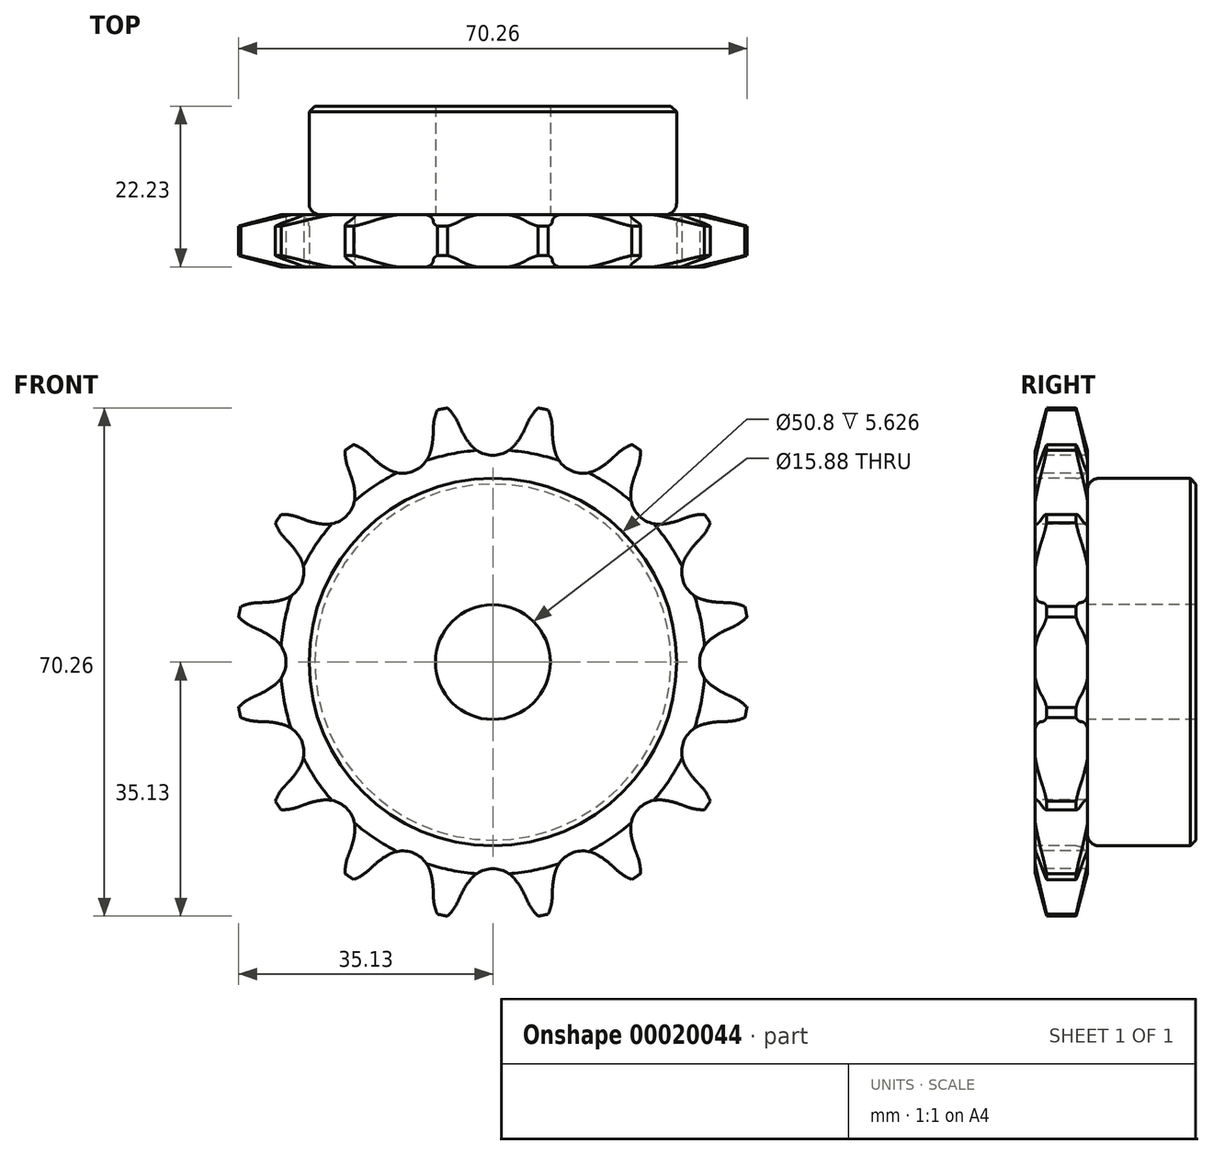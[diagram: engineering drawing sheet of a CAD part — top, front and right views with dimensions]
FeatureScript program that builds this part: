
annotation { "Feature Type Name" : "Feature", "Feature Type Description" : "" }
export const myFeature = defineFeature(function(context is Context, id is Id, definition is map)
    precondition{}
    {
        {
            var Q0;
            Q0=qCreatedBy(makeId("Right.planeOp"),FACE);
            var sketch = newSketch(context, id + "F0", { "sketchPlane" : qUnion([Q0])});
            skLineSegment(sketch, "E0", {"start": v(0, 0) * mm, "end": v(32.17, 0) * mm, "construction": true});
            skLineSegment(sketch, "E1.bottom", {"start": v(0, 7.94) * mm, "end": v(7.21, 7.94) * mm});
            skLineSegment(sketch, "E1.top", {"start": v(0, 35.69) * mm, "end": v(7.21, 35.69) * mm});
            skLineSegment(sketch, "E1.left", {"start": v(0, 7.94) * mm, "end": v(0, 35.69) * mm});
            skLineSegment(sketch, "E1.right", {"start": v(7.21, 7.94) * mm, "end": v(7.21, 35.69) * mm});
            skLineSegment(sketch, "E2.bottom", {"start": v(0, 7.94) * mm, "end": v(22.23, 7.94) * mm});
            skLineSegment(sketch, "E2.top", {"start": v(0, 25.4) * mm, "end": v(22.23, 25.4) * mm});
            skLineSegment(sketch, "E2.left", {"start": v(0, 7.94) * mm, "end": v(0, 25.4) * mm});
            skLineSegment(sketch, "E2.right", {"start": v(22.23, 7.94) * mm, "end": v(22.23, 25.4) * mm});
            skLineSegment(sketch, "E3.MirrorCS", {"start": v(0, -7.94) * mm, "end": v(0, -25.4) * mm});
            skLineSegment(sketch, "E4.MirrorCS", {"start": v(0, -7.94) * mm, "end": v(7.21, -7.94) * mm});
            skLineSegment(sketch, "E5.MirrorCS", {"start": v(0, -35.69) * mm, "end": v(7.21, -35.69) * mm});
            skLineSegment(sketch, "E6.MirrorCS", {"start": v(0, -7.94) * mm, "end": v(0, -35.69) * mm});
            skLineSegment(sketch, "E7.MirrorCS", {"start": v(7.21, -7.94) * mm, "end": v(7.21, -35.69) * mm});
            skLineSegment(sketch, "E8.MirrorCS", {"start": v(0, -7.94) * mm, "end": v(22.23, -7.94) * mm});
            skLineSegment(sketch, "E9.MirrorCS", {"start": v(0, -25.4) * mm, "end": v(22.23, -25.4) * mm});
            skLineSegment(sketch, "E10.MirrorCS", {"start": v(22.23, -7.94) * mm, "end": v(22.23, -25.4) * mm});
            skSolve(sketch);
        }
        {
            var Q0;
            {var subQ0=sQuery(id+"F0.wireOp",EDGE,"E2.left");Q0=makeQuery(id+"F0.imprint","IMPRINT",FACE,{"disambiguationData":[TD([[makeQuery(id+"F0.imprint","IMPRINT",EDGE,{"derivedFrom":subQ0}),-1.0]])]});}
            var Q1;
            {var subQ4=sQuery(id+"F0.wireOp",EDGE,"E1.top");Q1=makeQuery(id+"F0.imprint","IMPRINT",FACE,{"disambiguationData":[TD([[makeQuery(id+"F0.imprint","IMPRINT",EDGE,{"derivedFrom":subQ4}),-1.0]])]});}
            var Q2;
            {var subQ0=sQuery(id+"F0.wireOp",EDGE,"E2.right");Q2=makeQuery(id+"F0.imprint","IMPRINT",FACE,{"disambiguationData":[TD([[makeQuery(id+"F0.imprint","IMPRINT",EDGE,{"derivedFrom":subQ0}),1.0]])]});}
            var Q3;
            Q3=sQuery(id+"F0.wireOp",EDGE,"E0");
            revolve(context, id + "F1", {"entities" : qUnion([Q0, Q1, Q2]), "axis" : qUnion([Q3]), "revolveType" : RevolveType.FULL});
        }
        {
            var Q0;
            Q0=makeQuery(id+"F1.opRevolve","SWEPT_EDGE",EDGE,{"disambiguationData":[OSD([sQuery(id+"F0.wireOp",EDGE,"E1.right"),sQuery(id+"F0.wireOp",EDGE,"E2.top")])]});
            fillet(context, id + "F2", {"entities" : qUnion([Q0]), "radius" : 1.59 * mm, "tangentPropagation" : true, "allowEdgeOverflow" : false});
        }
        {
            var Q0;
            Q0=makeQuery(id+"F1.opRevolve","SWEPT_EDGE",EDGE,{"disambiguationData":[OSD([sQuery(id+"F0.wireOp",EDGE,"E2.top"),sQuery(id+"F0.wireOp",EDGE,"E2.right")])]});
            chamfer(context, id + "F3", {"entities" : qUnion([Q0]), "width" : 0.8 * mm, "tangentPropagation" : true});
        }
        {
            var Q0;
            Q0=makeQuery(id+"F1.opRevolve","SWEPT_EDGE",EDGE,{"disambiguationData":[OSD([sQuery(id+"F0.wireOp",EDGE,"E1.top"),sQuery(id+"F0.wireOp",EDGE,"E1.left")])]});
            var Q1;
            Q1=makeQuery(id+"F1.opRevolve","SWEPT_EDGE",EDGE,{"disambiguationData":[OSD([sQuery(id+"F0.wireOp",EDGE,"E1.top"),sQuery(id+"F0.wireOp",EDGE,"E1.right")])]});
            chamfer(context, id + "F4", {"entities" : qUnion([Q0, Q1]), "chamferType" : ChamferType.TWO_OFFSETS, "width1" : 6.35 * mm, "oppositeDirection" : false, "width2" : 1.57 * mm, "tangentPropagation" : true});
        }
        {
            var Q0;
            Q0=makeQuery(id+"F1.opRevolve","SWEPT_FACE",FACE,{"disambiguationData":[OSD([sQuery(id+"F0.wireOp",EDGE,"E1.left"),sQuery(id+"F0.wireOp",EDGE,"E2.left")])]});
            var sketch = newSketch(context, id + "F5", { "sketchPlane" : qUnion([Q0])});
            skCircle(sketch, "E11", {"center": v(0, 0) * mm, "radius": 32.55 * mm, "construction": true});
            skLineSegment(sketch, "E12", {"start": v(0, 0) * mm, "end": v(0, 32.55) * mm, "construction": true});
            skLineSegment(sketch, "E13", {"start": v(0, 32.55) * mm, "end": v(21.93, 32.55) * mm, "construction": true});
            skLineSegment(sketch, "E14", {"start": v(0, 32.55) * mm, "end": v(4.99, 36.55) * mm, "construction": true});
            skLineSegment(sketch, "E15", {"start": v(4.99, 36.55) * mm, "end": v(-4.46, 32.3) * mm, "construction": true});
            skLineSegment(sketch, "E16", {"start": v(-4.46, 32.3) * mm, "end": v(-4.81, 33.1) * mm});
            skLineSegment(sketch, "E17", {"start": v(0, 0) * mm, "end": v(-7.13, 35.84) * mm, "construction": true});
            skArc(sketch, "E18", {"start": v(-7.13, 35.84) * mm, "mid": v(-15.86, 26.14) * mm, "end": v(-4.81, 33.1) * mm, "construction": true});
            skArc(sketch, "E19", {"start": v(-4.81, 33.1) * mm, "mid": v(-5.78, 34.63) * mm, "end": v(-7.13, 35.84) * mm});
            skLineSegment(sketch, "E20", {"start": v(-4.81, 33.1) * mm, "end": v(-4.81, 33.1) * mm});
            skLineSegment(sketch, "E21", {"start": v(-4.81, 33.1) * mm, "end": v(-5.93, 35.58) * mm, "construction": true});
            skArc(sketch, "E22", {"start": v(-4.46, 32.3) * mm, "mid": v(-3.84, 31.14) * mm, "end": v(-3.1, 30.07) * mm});
            skArc(sketch, "E23", {"start": v(-3.1, 30.07) * mm, "mid": v(13.82, 41.97) * mm, "end": v(-4.46, 32.3) * mm, "construction": true});
            skArc(sketch, "E24.MirrorCS", {"start": v(4.81, 33.1) * mm, "mid": v(5.78, 34.63) * mm, "end": v(7.13, 35.84) * mm});
            skLineSegment(sketch, "E25.MirrorCS", {"start": v(4.46, 32.3) * mm, "end": v(4.81, 33.1) * mm});
            skArc(sketch, "E26.MirrorCS", {"start": v(4.46, 32.3) * mm, "mid": v(3.84, 31.14) * mm, "end": v(3.1, 30.07) * mm});
            skArc(sketch, "E27", {"start": v(-3.1, 30.07) * mm, "mid": v(0, 28.59) * mm, "end": v(3.1, 30.07) * mm});
            skArc(sketch, "E28", {"start": v(3.1, 30.07) * mm, "mid": v(0, 36.51) * mm, "end": v(-3.1, 30.07) * mm, "construction": true});
            skLineSegment(sketch, "E29.1.0", {"start": v(-16.48, 28.13) * mm, "end": v(-17.11, 28.73) * mm});
            skArc(sketch, "E29.1.1", {"start": v(-17.11, 28.73) * mm, "mid": v(-18.6, 29.78) * mm, "end": v(-20.3, 30.39) * mm});
            skArc(sketch, "E29.1.2", {"start": v(-16.48, 28.13) * mm, "mid": v(-15.47, 27.3) * mm, "end": v(-14.36, 26.6) * mm});
            skArc(sketch, "E29.1.3", {"start": v(-14.36, 26.6) * mm, "mid": v(-10.94, 26.41) * mm, "end": v(-8.65, 28.96) * mm});
            skArc(sketch, "E29.1.4", {"start": v(-8.24, 31.55) * mm, "mid": v(-8.37, 30.24) * mm, "end": v(-8.65, 28.96) * mm});
            skLineSegment(sketch, "E29.1.5", {"start": v(-8.24, 31.55) * mm, "end": v(-8.22, 32.41) * mm});
            skArc(sketch, "E29.1.6", {"start": v(-8.22, 32.41) * mm, "mid": v(-7.91, 34.2) * mm, "end": v(-7.13, 35.84) * mm});
            skLineSegment(sketch, "E29.2.0", {"start": v(-25.99, 19.69) * mm, "end": v(-26.8, 20) * mm});
            skArc(sketch, "E29.2.1", {"start": v(-26.8, 20) * mm, "mid": v(-28.57, 20.4) * mm, "end": v(-30.39, 20.3) * mm});
            skArc(sketch, "E29.2.2", {"start": v(-25.99, 19.69) * mm, "mid": v(-24.74, 19.3) * mm, "end": v(-23.45, 19.08) * mm});
            skArc(sketch, "E29.2.3", {"start": v(-23.45, 19.08) * mm, "mid": v(-20.21, 20.21) * mm, "end": v(-19.08, 23.45) * mm});
            skArc(sketch, "E29.2.4", {"start": v(-19.69, 25.99) * mm, "mid": v(-19.3, 24.74) * mm, "end": v(-19.08, 23.45) * mm});
            skLineSegment(sketch, "E29.2.5", {"start": v(-19.69, 25.99) * mm, "end": v(-20, 26.8) * mm});
            skArc(sketch, "E29.2.6", {"start": v(-20, 26.8) * mm, "mid": v(-20.4, 28.57) * mm, "end": v(-20.3, 30.39) * mm});
            skLineSegment(sketch, "E30.1.3.0", {"start": v(-31.55, 8.24) * mm, "end": v(-32.41, 8.22) * mm});
            skArc(sketch, "E30.3.3.0", {"start": v(-32.41, 8.22) * mm, "mid": v(-34.2, 7.91) * mm, "end": v(-35.84, 7.13) * mm});
            skArc(sketch, "E30.7.3.0", {"start": v(-31.55, 8.24) * mm, "mid": v(-30.24, 8.37) * mm, "end": v(-28.96, 8.65) * mm});
            skArc(sketch, "E30.11.3.0", {"start": v(-28.96, 8.65) * mm, "mid": v(-26.41, 10.94) * mm, "end": v(-26.6, 14.36) * mm});
            skArc(sketch, "E30.15.3.0", {"start": v(-28.13, 16.48) * mm, "mid": v(-27.3, 15.47) * mm, "end": v(-26.6, 14.36) * mm});
            skLineSegment(sketch, "E30.19.3.0", {"start": v(-28.13, 16.48) * mm, "end": v(-28.73, 17.11) * mm});
            skArc(sketch, "E30.22.3.0", {"start": v(-28.73, 17.11) * mm, "mid": v(-29.78, 18.6) * mm, "end": v(-30.39, 20.3) * mm});
            skLineSegment(sketch, "E30.1.4.0", {"start": v(-32.3, -4.46) * mm, "end": v(-33.1, -4.81) * mm});
            skArc(sketch, "E30.3.4.0", {"start": v(-33.1, -4.81) * mm, "mid": v(-34.63, -5.78) * mm, "end": v(-35.84, -7.13) * mm});
            skArc(sketch, "E30.7.4.0", {"start": v(-32.3, -4.46) * mm, "mid": v(-31.14, -3.84) * mm, "end": v(-30.07, -3.1) * mm});
            skArc(sketch, "E30.11.4.0", {"start": v(-30.07, -3.1) * mm, "mid": v(-28.59, 0) * mm, "end": v(-30.07, 3.1) * mm});
            skArc(sketch, "E30.15.4.0", {"start": v(-32.3, 4.46) * mm, "mid": v(-31.14, 3.84) * mm, "end": v(-30.07, 3.1) * mm});
            skLineSegment(sketch, "E30.19.4.0", {"start": v(-32.3, 4.46) * mm, "end": v(-33.1, 4.81) * mm});
            skArc(sketch, "E30.22.4.0", {"start": v(-33.1, 4.81) * mm, "mid": v(-34.63, 5.78) * mm, "end": v(-35.84, 7.13) * mm});
            skLineSegment(sketch, "E30.1.5.0", {"start": v(-28.13, -16.48) * mm, "end": v(-28.73, -17.11) * mm});
            skArc(sketch, "E30.3.5.0", {"start": v(-28.73, -17.11) * mm, "mid": v(-29.78, -18.6) * mm, "end": v(-30.39, -20.3) * mm});
            skArc(sketch, "E30.7.5.0", {"start": v(-28.13, -16.48) * mm, "mid": v(-27.3, -15.47) * mm, "end": v(-26.6, -14.36) * mm});
            skArc(sketch, "E30.11.5.0", {"start": v(-26.6, -14.36) * mm, "mid": v(-26.41, -10.94) * mm, "end": v(-28.96, -8.65) * mm});
            skArc(sketch, "E30.15.5.0", {"start": v(-31.55, -8.24) * mm, "mid": v(-30.24, -8.37) * mm, "end": v(-28.96, -8.65) * mm});
            skLineSegment(sketch, "E30.19.5.0", {"start": v(-31.55, -8.24) * mm, "end": v(-32.41, -8.22) * mm});
            skArc(sketch, "E30.22.5.0", {"start": v(-32.41, -8.22) * mm, "mid": v(-34.2, -7.91) * mm, "end": v(-35.84, -7.13) * mm});
            skLineSegment(sketch, "E30.1.6.0", {"start": v(-19.69, -25.99) * mm, "end": v(-20, -26.8) * mm});
            skArc(sketch, "E30.3.6.0", {"start": v(-20, -26.8) * mm, "mid": v(-20.4, -28.57) * mm, "end": v(-20.3, -30.39) * mm});
            skArc(sketch, "E30.7.6.0", {"start": v(-19.69, -25.99) * mm, "mid": v(-19.3, -24.74) * mm, "end": v(-19.08, -23.45) * mm});
            skArc(sketch, "E30.11.6.0", {"start": v(-19.08, -23.45) * mm, "mid": v(-20.21, -20.21) * mm, "end": v(-23.45, -19.08) * mm});
            skArc(sketch, "E30.15.6.0", {"start": v(-25.99, -19.69) * mm, "mid": v(-24.74, -19.3) * mm, "end": v(-23.45, -19.08) * mm});
            skLineSegment(sketch, "E30.19.6.0", {"start": v(-25.99, -19.69) * mm, "end": v(-26.8, -20) * mm});
            skArc(sketch, "E30.22.6.0", {"start": v(-26.8, -20) * mm, "mid": v(-28.57, -20.4) * mm, "end": v(-30.39, -20.3) * mm});
            skLineSegment(sketch, "E30.1.7.0", {"start": v(-8.24, -31.55) * mm, "end": v(-8.22, -32.41) * mm});
            skArc(sketch, "E30.3.7.0", {"start": v(-8.22, -32.41) * mm, "mid": v(-7.91, -34.2) * mm, "end": v(-7.13, -35.84) * mm});
            skArc(sketch, "E30.7.7.0", {"start": v(-8.24, -31.55) * mm, "mid": v(-8.37, -30.24) * mm, "end": v(-8.65, -28.96) * mm});
            skArc(sketch, "E30.11.7.0", {"start": v(-8.65, -28.96) * mm, "mid": v(-10.94, -26.41) * mm, "end": v(-14.36, -26.6) * mm});
            skArc(sketch, "E30.15.7.0", {"start": v(-16.48, -28.13) * mm, "mid": v(-15.47, -27.3) * mm, "end": v(-14.36, -26.6) * mm});
            skLineSegment(sketch, "E30.19.7.0", {"start": v(-16.48, -28.13) * mm, "end": v(-17.11, -28.73) * mm});
            skArc(sketch, "E30.22.7.0", {"start": v(-17.11, -28.73) * mm, "mid": v(-18.6, -29.78) * mm, "end": v(-20.3, -30.39) * mm});
            skLineSegment(sketch, "E30.1.8.0", {"start": v(4.46, -32.3) * mm, "end": v(4.81, -33.1) * mm});
            skArc(sketch, "E30.3.8.0", {"start": v(4.81, -33.1) * mm, "mid": v(5.78, -34.63) * mm, "end": v(7.13, -35.84) * mm});
            skArc(sketch, "E30.7.8.0", {"start": v(4.46, -32.3) * mm, "mid": v(3.84, -31.14) * mm, "end": v(3.1, -30.07) * mm});
            skArc(sketch, "E30.11.8.0", {"start": v(3.1, -30.07) * mm, "mid": v(0, -28.59) * mm, "end": v(-3.1, -30.07) * mm});
            skArc(sketch, "E30.15.8.0", {"start": v(-4.46, -32.3) * mm, "mid": v(-3.84, -31.14) * mm, "end": v(-3.1, -30.07) * mm});
            skLineSegment(sketch, "E30.19.8.0", {"start": v(-4.46, -32.3) * mm, "end": v(-4.81, -33.1) * mm});
            skArc(sketch, "E30.22.8.0", {"start": v(-4.81, -33.1) * mm, "mid": v(-5.78, -34.63) * mm, "end": v(-7.13, -35.84) * mm});
            skLineSegment(sketch, "E30.1.9.0", {"start": v(16.48, -28.13) * mm, "end": v(17.11, -28.73) * mm});
            skArc(sketch, "E30.3.9.0", {"start": v(17.11, -28.73) * mm, "mid": v(18.6, -29.78) * mm, "end": v(20.3, -30.39) * mm});
            skArc(sketch, "E30.7.9.0", {"start": v(16.48, -28.13) * mm, "mid": v(15.47, -27.3) * mm, "end": v(14.36, -26.6) * mm});
            skArc(sketch, "E30.11.9.0", {"start": v(14.36, -26.6) * mm, "mid": v(10.94, -26.41) * mm, "end": v(8.65, -28.96) * mm});
            skArc(sketch, "E30.15.9.0", {"start": v(8.24, -31.55) * mm, "mid": v(8.37, -30.24) * mm, "end": v(8.65, -28.96) * mm});
            skLineSegment(sketch, "E30.19.9.0", {"start": v(8.24, -31.55) * mm, "end": v(8.22, -32.41) * mm});
            skArc(sketch, "E30.22.9.0", {"start": v(8.22, -32.41) * mm, "mid": v(7.91, -34.2) * mm, "end": v(7.13, -35.84) * mm});
            skLineSegment(sketch, "E30.1.10.0", {"start": v(25.99, -19.69) * mm, "end": v(26.8, -20) * mm});
            skArc(sketch, "E30.3.10.0", {"start": v(26.8, -20) * mm, "mid": v(28.57, -20.4) * mm, "end": v(30.39, -20.3) * mm});
            skArc(sketch, "E30.7.10.0", {"start": v(25.99, -19.69) * mm, "mid": v(24.74, -19.3) * mm, "end": v(23.45, -19.08) * mm});
            skArc(sketch, "E30.11.10.0", {"start": v(23.45, -19.08) * mm, "mid": v(20.21, -20.21) * mm, "end": v(19.08, -23.45) * mm});
            skArc(sketch, "E30.15.10.0", {"start": v(19.69, -25.99) * mm, "mid": v(19.3, -24.74) * mm, "end": v(19.08, -23.45) * mm});
            skLineSegment(sketch, "E30.19.10.0", {"start": v(19.69, -25.99) * mm, "end": v(20, -26.8) * mm});
            skArc(sketch, "E30.22.10.0", {"start": v(20, -26.8) * mm, "mid": v(20.4, -28.57) * mm, "end": v(20.3, -30.39) * mm});
            skLineSegment(sketch, "E30.1.11.0", {"start": v(31.55, -8.24) * mm, "end": v(32.41, -8.22) * mm});
            skArc(sketch, "E30.3.11.0", {"start": v(32.41, -8.22) * mm, "mid": v(34.2, -7.91) * mm, "end": v(35.84, -7.13) * mm});
            skArc(sketch, "E30.7.11.0", {"start": v(31.55, -8.24) * mm, "mid": v(30.24, -8.37) * mm, "end": v(28.96, -8.65) * mm});
            skArc(sketch, "E30.11.11.0", {"start": v(28.96, -8.65) * mm, "mid": v(26.41, -10.94) * mm, "end": v(26.6, -14.36) * mm});
            skArc(sketch, "E30.15.11.0", {"start": v(28.13, -16.48) * mm, "mid": v(27.3, -15.47) * mm, "end": v(26.6, -14.36) * mm});
            skLineSegment(sketch, "E30.19.11.0", {"start": v(28.13, -16.48) * mm, "end": v(28.73, -17.11) * mm});
            skArc(sketch, "E30.22.11.0", {"start": v(28.73, -17.11) * mm, "mid": v(29.78, -18.6) * mm, "end": v(30.39, -20.3) * mm});
            skLineSegment(sketch, "E30.1.12.0", {"start": v(32.3, 4.46) * mm, "end": v(33.1, 4.81) * mm});
            skArc(sketch, "E30.3.12.0", {"start": v(33.1, 4.81) * mm, "mid": v(34.63, 5.78) * mm, "end": v(35.84, 7.13) * mm});
            skArc(sketch, "E30.7.12.0", {"start": v(32.3, 4.46) * mm, "mid": v(31.14, 3.84) * mm, "end": v(30.07, 3.1) * mm});
            skArc(sketch, "E30.11.12.0", {"start": v(30.07, 3.1) * mm, "mid": v(28.59, 0) * mm, "end": v(30.07, -3.1) * mm});
            skArc(sketch, "E30.15.12.0", {"start": v(32.3, -4.46) * mm, "mid": v(31.14, -3.84) * mm, "end": v(30.07, -3.1) * mm});
            skLineSegment(sketch, "E30.19.12.0", {"start": v(32.3, -4.46) * mm, "end": v(33.1, -4.81) * mm});
            skArc(sketch, "E30.22.12.0", {"start": v(33.1, -4.81) * mm, "mid": v(34.63, -5.78) * mm, "end": v(35.84, -7.13) * mm});
            skLineSegment(sketch, "E30.1.13.0", {"start": v(28.13, 16.48) * mm, "end": v(28.73, 17.11) * mm});
            skArc(sketch, "E30.3.13.0", {"start": v(28.73, 17.11) * mm, "mid": v(29.78, 18.6) * mm, "end": v(30.39, 20.3) * mm});
            skArc(sketch, "E30.7.13.0", {"start": v(28.13, 16.48) * mm, "mid": v(27.3, 15.47) * mm, "end": v(26.6, 14.36) * mm});
            skArc(sketch, "E30.11.13.0", {"start": v(26.6, 14.36) * mm, "mid": v(26.41, 10.94) * mm, "end": v(28.96, 8.65) * mm});
            skArc(sketch, "E30.15.13.0", {"start": v(31.55, 8.24) * mm, "mid": v(30.24, 8.37) * mm, "end": v(28.96, 8.65) * mm});
            skLineSegment(sketch, "E30.19.13.0", {"start": v(31.55, 8.24) * mm, "end": v(32.41, 8.22) * mm});
            skArc(sketch, "E30.22.13.0", {"start": v(32.41, 8.22) * mm, "mid": v(34.2, 7.91) * mm, "end": v(35.84, 7.13) * mm});
            skLineSegment(sketch, "E30.1.14.0", {"start": v(19.69, 25.99) * mm, "end": v(20, 26.8) * mm});
            skArc(sketch, "E30.3.14.0", {"start": v(20, 26.8) * mm, "mid": v(20.4, 28.57) * mm, "end": v(20.3, 30.39) * mm});
            skArc(sketch, "E30.7.14.0", {"start": v(19.69, 25.99) * mm, "mid": v(19.3, 24.74) * mm, "end": v(19.08, 23.45) * mm});
            skArc(sketch, "E30.11.14.0", {"start": v(19.08, 23.45) * mm, "mid": v(20.21, 20.21) * mm, "end": v(23.45, 19.08) * mm});
            skArc(sketch, "E30.15.14.0", {"start": v(25.99, 19.69) * mm, "mid": v(24.74, 19.3) * mm, "end": v(23.45, 19.08) * mm});
            skLineSegment(sketch, "E30.19.14.0", {"start": v(25.99, 19.69) * mm, "end": v(26.8, 20) * mm});
            skArc(sketch, "E30.22.14.0", {"start": v(26.8, 20) * mm, "mid": v(28.57, 20.4) * mm, "end": v(30.39, 20.3) * mm});
            skLineSegment(sketch, "E30.1.15.0", {"start": v(8.24, 31.55) * mm, "end": v(8.22, 32.41) * mm});
            skArc(sketch, "E30.3.15.0", {"start": v(8.22, 32.41) * mm, "mid": v(7.91, 34.2) * mm, "end": v(7.13, 35.84) * mm});
            skArc(sketch, "E30.7.15.0", {"start": v(8.24, 31.55) * mm, "mid": v(8.37, 30.24) * mm, "end": v(8.65, 28.96) * mm});
            skArc(sketch, "E30.11.15.0", {"start": v(8.65, 28.96) * mm, "mid": v(10.94, 26.41) * mm, "end": v(14.36, 26.6) * mm});
            skArc(sketch, "E30.15.15.0", {"start": v(16.48, 28.13) * mm, "mid": v(15.47, 27.3) * mm, "end": v(14.36, 26.6) * mm});
            skLineSegment(sketch, "E30.19.15.0", {"start": v(16.48, 28.13) * mm, "end": v(17.11, 28.73) * mm});
            skArc(sketch, "E30.22.15.0", {"start": v(17.11, 28.73) * mm, "mid": v(18.6, 29.78) * mm, "end": v(20.3, 30.39) * mm});
            skSolve(sketch);
        }
        {
            var Q0;
            Q0=qSketchRegion(id+"F5",true);
            extrude(context, id + "F6", {"entities" : qUnion([Q0]), "operationType" : NewBodyOperationType.INTERSECT, "endBound" : BoundingType.THROUGH_ALL, "oppositeDirection" : true, "depth" : 25.4 * mm});
        }
    });
